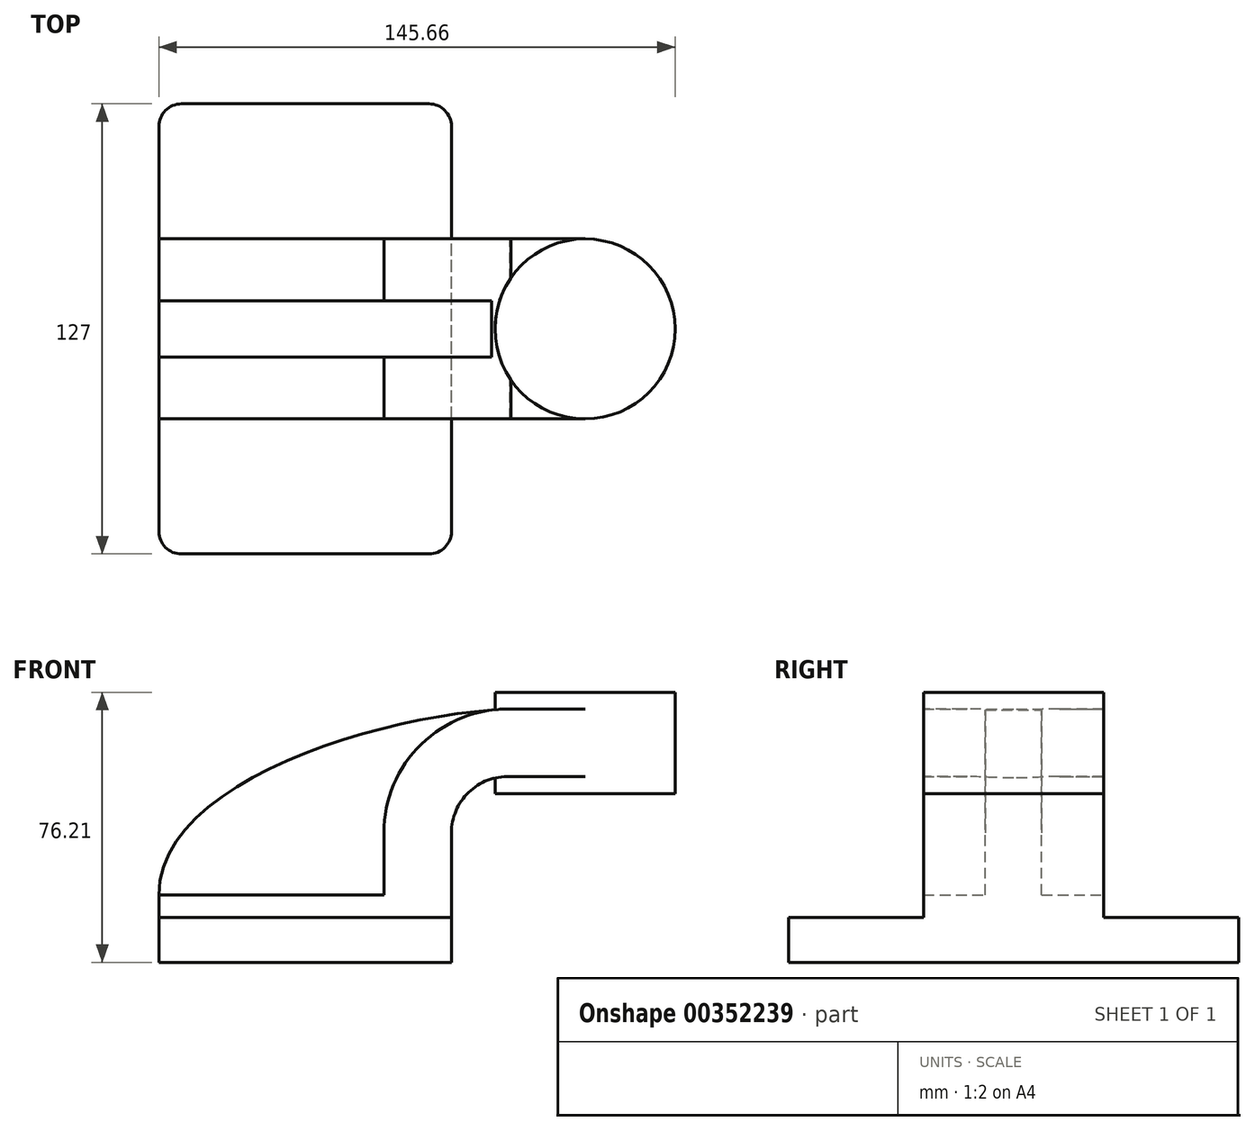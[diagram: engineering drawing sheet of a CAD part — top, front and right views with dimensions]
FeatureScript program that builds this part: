
annotation { "Feature Type Name" : "Feature", "Feature Type Description" : "" }
export const myFeature = defineFeature(function(context is Context, id is Id, definition is map)
    precondition{}
    {
        {
            var Q0;
            Q0=qCreatedBy(makeId("Front.planeOp"),FACE);
            var sketch = newSketch(context, id + "F0", { "sketchPlane" : qUnion([Q0])});
            skLineSegment(sketch, "E0.bottom", {"start": v(-41.28, 9.52) * mm, "end": v(41.28, 9.53) * mm});
            skLineSegment(sketch, "E0.top", {"start": v(-41.28, -9.53) * mm, "end": v(41.28, -9.53) * mm});
            skLineSegment(sketch, "E0.left", {"start": v(-41.28, 9.52) * mm, "end": v(-41.28, -9.53) * mm});
            skLineSegment(sketch, "E0.right", {"start": v(41.28, 9.53) * mm, "end": v(41.28, -9.52) * mm});
            skPoint(sketch, "E0.middle", {"position": v(0, 0) * mm});
            skLineSegment(sketch, "E1.bottom", {"start": v(104.38, 66.67) * mm, "end": v(53.58, 66.67) * mm});
            skLineSegment(sketch, "E1.top", {"start": v(104.38, 38.1) * mm, "end": v(53.58, 38.1) * mm});
            skLineSegment(sketch, "E1.left", {"start": v(104.38, 66.67) * mm, "end": v(104.38, 38.1) * mm});
            skLineSegment(sketch, "E1.right", {"start": v(53.58, 66.67) * mm, "end": v(53.58, 38.1) * mm});
            skPoint(sketch, "E1.middle", {"position": v(78.98, 52.39) * mm});
            skLineSegment(sketch, "E2", {"start": v(41.27, 9.53) * mm, "end": v(41.27, 27.01) * mm});
            skArc(sketch, "E3", {"start": v(41.27, 27.01) * mm, "mid": v(46.14, 38.45) * mm, "end": v(57.75, 42.88) * mm});
            skLineSegment(sketch, "E4", {"start": v(57.75, 42.88) * mm, "end": v(85.73, 42.88) * mm});
            skLineSegment(sketch, "E5.0", {"start": v(58.04, 61.93) * mm, "end": v(85.73, 61.93) * mm});
            skArc(sketch, "E5.1", {"start": v(22.22, 27.01) * mm, "mid": v(32.77, 52.02) * mm, "end": v(58.04, 61.93) * mm});
            skLineSegment(sketch, "E5.2", {"start": v(22.22, 9.53) * mm, "end": v(22.22, 27.01) * mm});
            skLineSegment(sketch, "E6.0", {"start": v(-41.28, 3.17) * mm, "end": v(41.28, 3.18) * mm});
            skLineSegment(sketch, "E7", {"start": v(78.98, 38.1) * mm, "end": v(78.98, 66.67) * mm});
            skFitSpline(sketch, "E8", {"points": [v(-41.28, 9.52) * mm, v(58.04, 61.93) * mm], "startDerivative": vector(-0.2, 97.95) * mm, "endDerivative": vector(103.31, 3) * mm});
            skSolve(sketch);
        }
        {
            var Q0;
            {var subQ0=sQuery(id+"F0.wireOp",EDGE,"E0.top");Q0=makeQuery(id+"F0.imprint","IMPRINT",FACE,{"disambiguationData":[TD([[makeQuery(id+"F0.imprint","IMPRINT",EDGE,{"derivedFrom":subQ0}),1.0]])]});}
            extrude(context, id + "F1", {"entities" : qUnion([Q0]), "endBound" : BoundingType.SYMMETRIC, "depth" : 127 * mm});
        }
        {
            var Q0;
            {var subQ0=sQuery(id+"F0.wireOp",EDGE,"E0.top");Q0=makeQuery(id+"F0.imprint","IMPRINT",FACE,{"disambiguationData":[TD([[makeQuery(id+"F0.imprint","IMPRINT",EDGE,{"derivedFrom":subQ0}),1.0]])]});}
            var Q1;
            {var subQ0=sQuery(id+"F0.wireOp",EDGE,"E5.1");var subQ1=sQuery(id+"F0.wireOp",EDGE,"E1.right");var subQ2=makeQuery(id+"F0.imprint","INTERSECT",VERTEX,{"derivedFrom":[subQ1,subQ0]});Q1=makeQuery(id+"F0.imprint","IMPRINT",FACE,{"disambiguationData":[TD([[makeQuery(id+"F0.imprint","IMPRINT",EDGE,{"disambiguationData":[TD([[subQ2,-1.0]])],"derivedFrom":subQ1}),-1.0]])]});}
            var Q2;
            {var subQ3=sQuery(id+"F0.wireOp",EDGE,"E6.0");Q2=makeQuery(id+"F0.imprint","IMPRINT",FACE,{"disambiguationData":[TD([[makeQuery(id+"F0.imprint","IMPRINT",EDGE,{"derivedFrom":subQ3}),1.0]])]});}
            var Q3;
            {var subQ0=sQuery(id+"F0.wireOp",EDGE,"E5.1");var subQ1=sQuery(id+"F0.wireOp",EDGE,"E1.right");var subQ2=makeQuery(id+"F0.imprint","INTERSECT",VERTEX,{"derivedFrom":[subQ1,subQ0]});Q3=makeQuery(id+"F0.imprint","IMPRINT",FACE,{"disambiguationData":[TD([[makeQuery(id+"F0.imprint","IMPRINT",EDGE,{"disambiguationData":[TD([[subQ2,-1.0]])],"derivedFrom":subQ1}),1.0]])]});}
            var Q4;
            {var subQ1=sQuery(id+"F0.wireOp",EDGE,"E2");Q4=makeQuery(id+"F0.imprint","IMPRINT",FACE,{"disambiguationData":[TD([[makeQuery(id+"F0.imprint","IMPRINT",EDGE,{"derivedFrom":subQ1}),1.0]])]});}
            var Q5;
            {var subQ5=sQuery(id+"F0.wireOp",EDGE,"E1.right");var subQ8=sQuery(id+"F0.wireOp",EDGE,"E3");var subQ10=makeQuery(id+"F0.imprint","INTERSECT",VERTEX,{"derivedFrom":[subQ5,subQ8]});Q5=makeQuery(id+"F0.imprint","IMPRINT",FACE,{"disambiguationData":[TD([[makeQuery(id+"F0.imprint","IMPRINT",EDGE,{"disambiguationData":[TD([[subQ10,1.0]])],"derivedFrom":subQ5}),1.0]])]});}
            extrude(context, id + "F2", {"entities" : qUnion([Q0, Q1, Q2, Q3, Q4, Q5]), "operationType" : NewBodyOperationType.ADD, "endBound" : BoundingType.SYMMETRIC, "depth" : 50.8 * mm});
        }
        {
            var Q0;
            {var subQ0=sQuery(id+"F0.wireOp",EDGE,"E0.top");Q0=makeQuery(id+"F0.imprint","IMPRINT",FACE,{"disambiguationData":[TD([[makeQuery(id+"F0.imprint","IMPRINT",EDGE,{"derivedFrom":subQ0}),1.0]])]});}
            var Q1;
            {var subQ3=sQuery(id+"F0.wireOp",EDGE,"E5.2");Q1=makeQuery(id+"F0.imprint","IMPRINT",FACE,{"disambiguationData":[TD([[makeQuery(id+"F0.imprint","IMPRINT",EDGE,{"derivedFrom":subQ3}),1.0]])]});}
            var Q2;
            {var subQ0=sQuery(id+"F0.wireOp",EDGE,"E5.1");var subQ1=sQuery(id+"F0.wireOp",EDGE,"E1.right");var subQ2=makeQuery(id+"F0.imprint","INTERSECT",VERTEX,{"derivedFrom":[subQ1,subQ0]});Q2=makeQuery(id+"F0.imprint","IMPRINT",FACE,{"disambiguationData":[TD([[makeQuery(id+"F0.imprint","IMPRINT",EDGE,{"disambiguationData":[TD([[subQ2,-1.0]])],"derivedFrom":subQ1}),-1.0]])]});}
            var Q3;
            {var subQ3=sQuery(id+"F0.wireOp",EDGE,"E6.0");Q3=makeQuery(id+"F0.imprint","IMPRINT",FACE,{"disambiguationData":[TD([[makeQuery(id+"F0.imprint","IMPRINT",EDGE,{"derivedFrom":subQ3}),1.0]])]});}
            var Q4;
            {var subQ0=sQuery(id+"F0.wireOp",EDGE,"E5.1");var subQ1=sQuery(id+"F0.wireOp",EDGE,"E1.right");var subQ2=makeQuery(id+"F0.imprint","INTERSECT",VERTEX,{"derivedFrom":[subQ1,subQ0]});Q4=makeQuery(id+"F0.imprint","IMPRINT",FACE,{"disambiguationData":[TD([[makeQuery(id+"F0.imprint","IMPRINT",EDGE,{"disambiguationData":[TD([[subQ2,-1.0]])],"derivedFrom":subQ1}),1.0]])]});}
            var Q5;
            {var subQ1=sQuery(id+"F0.wireOp",EDGE,"E2");Q5=makeQuery(id+"F0.imprint","IMPRINT",FACE,{"disambiguationData":[TD([[makeQuery(id+"F0.imprint","IMPRINT",EDGE,{"derivedFrom":subQ1}),1.0]])]});}
            var Q6;
            {var subQ5=sQuery(id+"F0.wireOp",EDGE,"E1.right");var subQ8=sQuery(id+"F0.wireOp",EDGE,"E3");var subQ10=makeQuery(id+"F0.imprint","INTERSECT",VERTEX,{"derivedFrom":[subQ5,subQ8]});Q6=makeQuery(id+"F0.imprint","IMPRINT",FACE,{"disambiguationData":[TD([[makeQuery(id+"F0.imprint","IMPRINT",EDGE,{"disambiguationData":[TD([[subQ10,1.0]])],"derivedFrom":subQ5}),1.0]])]});}
            extrude(context, id + "F3", {"entities" : qUnion([Q0, Q1, Q2, Q3, Q4, Q5, Q6]), "operationType" : NewBodyOperationType.ADD, "endBound" : BoundingType.SYMMETRIC, "depth" : 15.88 * mm});
        }
        {
            var Q0;
            {var subQ4=sQuery(id+"F0.wireOp",EDGE,"E1.left");Q0=makeQuery(id+"F0.imprint","IMPRINT",FACE,{"disambiguationData":[TD([[makeQuery(id+"F0.imprint","IMPRINT",EDGE,{"derivedFrom":subQ4}),-1.0]])]});}
            var Q1;
            Q1=sQuery(id+"F0.wireOp",EDGE,"E7");
            revolve(context, id + "F4", {"operationType" : NewBodyOperationType.ADD, "entities" : qUnion([Q0]), "axis" : qUnion([Q1]), "revolveType" : RevolveType.FULL});
        }
        {
            var Q0;
            Q0=makeQuery(id+"F1.opExtrude","CAP_EDGE",EDGE,{"disambiguationData":[OSD([sQuery(id+"F0.wireOp",EDGE,"E0.right")])],"isStart":false});
            var Q1;
            Q1=makeQuery(id+"F1.opExtrude","CAP_EDGE",EDGE,{"disambiguationData":[OSD([sQuery(id+"F0.wireOp",EDGE,"E0.left")])],"isStart":false});
            var Q2;
            Q2=makeQuery(id+"F1.opExtrude","CAP_EDGE",EDGE,{"disambiguationData":[OSD([sQuery(id+"F0.wireOp",EDGE,"E0.right")])],"isStart":true});
            var Q3;
            Q3=makeQuery(id+"F1.opExtrude","CAP_EDGE",EDGE,{"disambiguationData":[OSD([sQuery(id+"F0.wireOp",EDGE,"E0.left")])],"isStart":true});
            fillet(context, id + "F5", {"entities" : qUnion([Q0, Q1, Q2, Q3]), "radius" : 6.35 * mm, "tangentPropagation" : true, "allowEdgeOverflow" : false});
        }
    });
